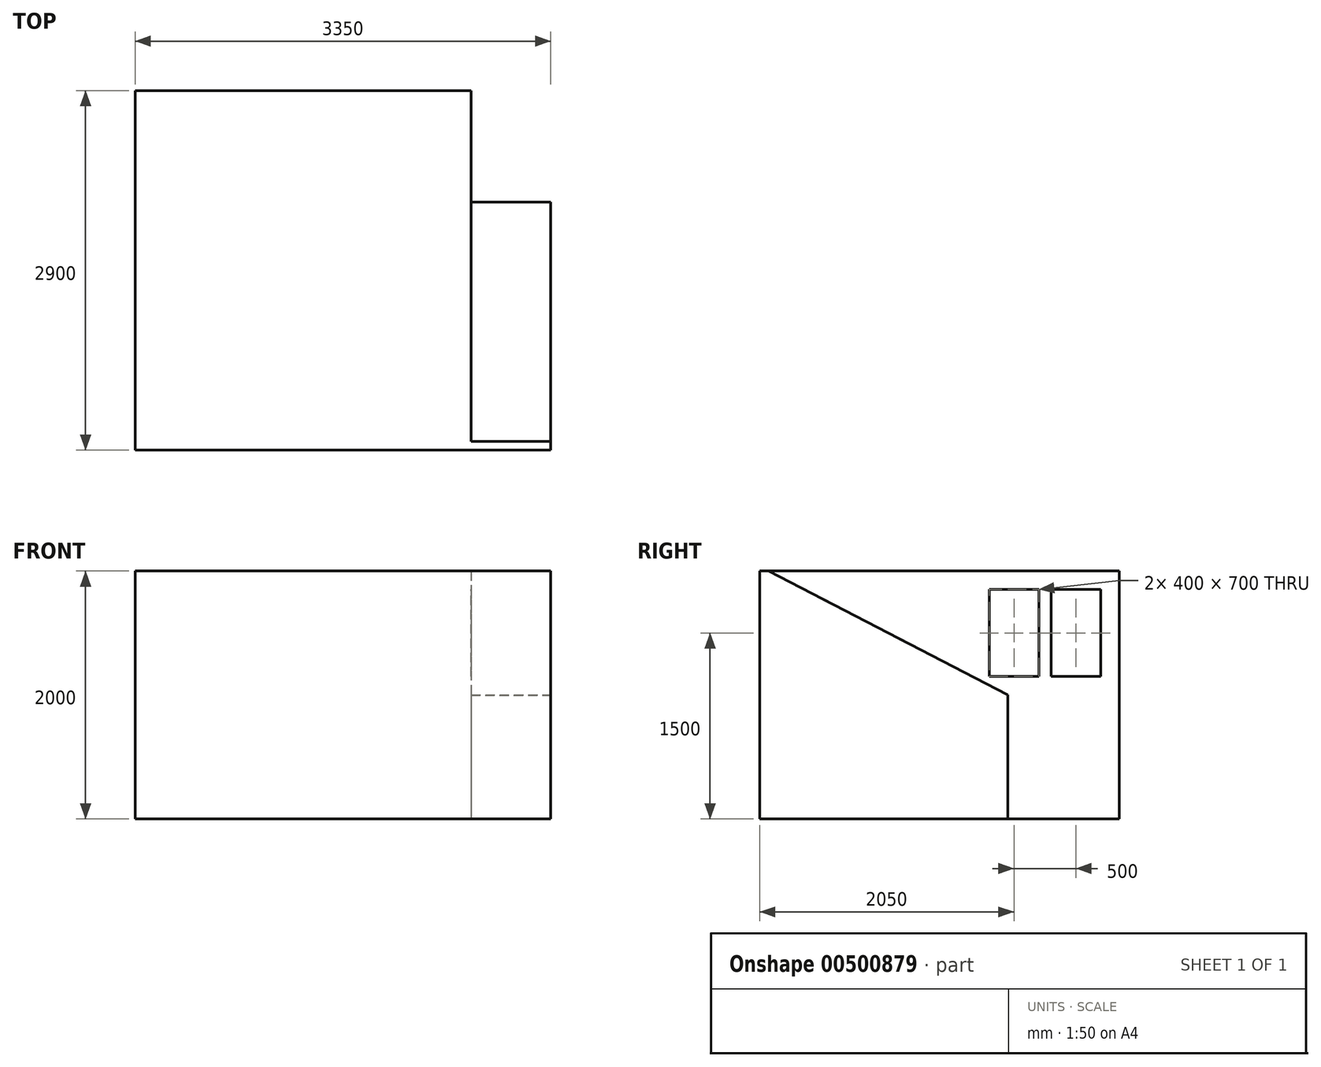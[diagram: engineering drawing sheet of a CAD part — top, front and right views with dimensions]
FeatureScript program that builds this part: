
annotation { "Feature Type Name" : "Feature", "Feature Type Description" : "" }
export const myFeature = defineFeature(function(context is Context, id is Id, definition is map)
    precondition{}
    {
        {
            var Q0;
            Q0=qCreatedBy(makeId("Top.planeOp"),FACE);
            var sketch = newSketch(context, id + "F0", { "sketchPlane" : qUnion([Q0])});
            skLineSegment(sketch, "E0.bottom", {"start": v(0, 10.3) * mm, "end": v(3350, 10.3) * mm});
            skLineSegment(sketch, "E0.top", {"start": v(0, 2910.3) * mm, "end": v(3350, 2910.3) * mm});
            skLineSegment(sketch, "E0.left", {"start": v(0, 10.3) * mm, "end": v(0, 2910.3) * mm});
            skLineSegment(sketch, "E0.right", {"start": v(3350, 10.3) * mm, "end": v(3350, 2910.3) * mm});
            skSolve(sketch);
        }
        {
            var Q0;
            Q0 = qSketchRegion(id + "F0", true);
            extrude(context, id + "F1", {"entities" : qUnion([Q0]), "depth" : 2000 * mm, "offsetDistance" : 25 * mm});
        }
        {
            var Q0;
            Q0=makeQuery(id+"F1.opExtrude","CAP_FACE",FACE,{"disambiguationData":[OSD([sQuery(id+"F0.wireOp",EDGE,"E0.bottom"),sQuery(id+"F0.wireOp",EDGE,"E0.top"),sQuery(id+"F0.wireOp",EDGE,"E0.left"),sQuery(id+"F0.wireOp",EDGE,"E0.right")])],"isStart":false});
            var sketch = newSketch(context, id + "F2", { "sketchPlane" : qUnion([Q0])});
            skLineSegment(sketch, "E1", {"start": v(1030, 2910.3) * mm, "end": v(1030, 80.3) * mm});
            skLineSegment(sketch, "E2", {"start": v(1030, 80.3) * mm, "end": v(3350, 80.3) * mm});
            skLineSegment(sketch, "E3", {"start": v(2310, 2910.3) * mm, "end": v(2310, 2010.3) * mm});
            skLineSegment(sketch, "E4", {"start": v(2310, 2010.3) * mm, "end": v(3350, 2010.3) * mm});
            skLineSegment(sketch, "E5", {"start": v(1030, 80.3) * mm, "end": v(2310, 2010.3) * mm});
            skSolve(sketch);
        }
        {
            var Q0;
            Q0=sQuery(id+"F2.wireOp",EDGE,"E5");
            cPlane(context, id + "F3", {"entities" : qUnion([Q0]), "cplaneType" : CPlaneType.LINE_ANGLE, "offset" : 25 * mm, "angle" : 90 * degree, "width" : 150 * mm, "height" : 150 * mm});
        }
        {
            var Q0;
            Q0=makeQuery(id+"F1.opExtrude","SWEPT_FACE",FACE,{"disambiguationData":[OSD([sQuery(id+"F0.wireOp",EDGE,"E0.right")])]});
            var sketch = newSketch(context, id + "F4", { "sketchPlane" : qUnion([Q0])});
            skLineSegment(sketch, "E6", {"start": v(80.3, 2000) * mm, "end": v(2010.3, 1000) * mm});
            skLineSegment(sketch, "E7", {"start": v(2910.3, 1000) * mm, "end": v(2910.3, 2000) * mm});
            skLineSegment(sketch, "E8", {"start": v(2910.3, 2000) * mm, "end": v(80.3, 2000) * mm});
            skLineSegment(sketch, "E9", {"start": v(2010.3, 1000) * mm, "end": v(2010.3, 0) * mm});
            skLineSegment(sketch, "E10", {"start": v(2010.3, 0) * mm, "end": v(2910.3, 0) * mm});
            skLineSegment(sketch, "E11", {"start": v(2910.3, 0) * mm, "end": v(2910.3, 1000) * mm});
            skSolve(sketch);
        }
        {
            var Q0;
            Q0 = qSketchRegion(id + "F4", true);
            var Q1;
            Q1=qCreatedBy(id+"F3.planeOp",FACE);
            extrude(context, id + "F5", {"entities" : qUnion([Q0]), "operationType" : NewBodyOperationType.REMOVE, "endBound" : BoundingType.UP_TO_SURFACE, "oppositeDirection" : true, "depth" : 25 * mm, "endBoundEntityFace" : qUnion([Q1]), "offsetDistance" : 25 * mm});
        }
        {
            var Q0;
            Q0=makeQuery(id+"F1.opExtrude","SWEPT_FACE",FACE,{"disambiguationData":[OSD([sQuery(id+"F0.wireOp",EDGE,"E0.top")])]});
            var sketch = newSketch(context, id + "F6", { "sketchPlane" : qUnion([Q0])});
            skLineSegment(sketch, "E12", {"start": v(-1030, 2000) * mm, "end": v(-2310, 1000) * mm});
            skLineSegment(sketch, "E13", {"start": v(-2906.9, 2000) * mm, "end": v(-1030, 2000) * mm});
            skLineSegment(sketch, "E14", {"start": v(-2310, 1000) * mm, "end": v(-2310, 0) * mm});
            skLineSegment(sketch, "E15", {"start": v(-2310, 0) * mm, "end": v(-2906.9, 0) * mm});
            skLineSegment(sketch, "E16", {"start": v(-2906.9, 0) * mm, "end": v(-2906.9, 2000) * mm});
            skSolve(sketch);
        }
        {
            var Q0;
            Q0 = qSketchRegion(id + "F6", true);
            var Q1;
            Q1=qCreatedBy(id+"F3.planeOp",FACE);
            extrude(context, id + "F7", {"entities" : qUnion([Q0]), "operationType" : NewBodyOperationType.REMOVE, "endBound" : BoundingType.UP_TO_SURFACE, "oppositeDirection" : true, "depth" : 25 * mm, "endBoundEntityFace" : qUnion([Q1]), "offsetDistance" : 25 * mm});
        }
        {
            var Q0;
            Q0=makeQuery(id+"F1.opExtrude","SWEPT_FACE",FACE,{"disambiguationData":[OSD([sQuery(id+"F0.wireOp",EDGE,"E0.top")])]});
            var sketch = newSketch(context, id + "F8", { "sketchPlane" : qUnion([Q0])});
            skLineSegment(sketch, "E17", {"start": v(-1030, 2000) * mm, "end": v(-2310, 1000) * mm});
            skLineSegment(sketch, "E18", {"start": v(-2710, 2000) * mm, "end": v(-1030, 2000) * mm});
            skLineSegment(sketch, "E19", {"start": v(-2710, 2000) * mm, "end": v(-2710, 0) * mm});
            skLineSegment(sketch, "E20", {"start": v(-2710, 0) * mm, "end": v(-2310, 0) * mm});
            skLineSegment(sketch, "E21", {"start": v(-2310, 0) * mm, "end": v(-2310, 1000) * mm});
            skSolve(sketch);
        }
        {
            var Q0;
            Q0 = qSketchRegion(id + "F8", true);
            extrude(context, id + "F9", {"entities" : qUnion([Q0]), "operationType" : NewBodyOperationType.ADD, "endBound" : BoundingType.UP_TO_NEXT, "oppositeDirection" : true, "depth" : 25 * mm, "offsetDistance" : 25 * mm});
        }
        {
            var Q0;
            Q0=makeQuery(id+"F1.opExtrude","CAP_FACE",FACE,{"disambiguationData":[OSD([sQuery(id+"F0.wireOp",EDGE,"E0.bottom"),sQuery(id+"F0.wireOp",EDGE,"E0.top"),sQuery(id+"F0.wireOp",EDGE,"E0.left"),sQuery(id+"F0.wireOp",EDGE,"E0.right")])],"isStart":true});
            shell(context, id + "F10", {"entities" : qUnion([Q0]), "thickness" : 2.5 * mm});
        }
        {
            var Q0;
            Q0=makeQuery(id+"F9.opExtrude","SWEPT_FACE",FACE,{"disambiguationData":[OSD([sQuery(id+"F8.wireOp",EDGE,"E19")])]});
            var sketch = newSketch(context, id + "F11", { "sketchPlane" : qUnion([Q0])});
            skLineSegment(sketch, "E22.bottom", {"start": v(2760.3, 1850) * mm, "end": v(2360.3, 1850) * mm});
            skLineSegment(sketch, "E22.top", {"start": v(2760.3, 1150) * mm, "end": v(2360.3, 1150) * mm});
            skLineSegment(sketch, "E22.left", {"start": v(2760.3, 1850) * mm, "end": v(2760.3, 1150) * mm});
            skLineSegment(sketch, "E22.right", {"start": v(2360.3, 1850) * mm, "end": v(2360.3, 1150) * mm});
            skLineSegment(sketch, "E23.bottom", {"start": v(2260.3, 1850) * mm, "end": v(1860.3, 1850) * mm});
            skLineSegment(sketch, "E23.top", {"start": v(2260.3, 1150) * mm, "end": v(1860.3, 1150) * mm});
            skLineSegment(sketch, "E23.left", {"start": v(2260.3, 1850) * mm, "end": v(2260.3, 1150) * mm});
            skLineSegment(sketch, "E23.right", {"start": v(1860.3, 1850) * mm, "end": v(1860.3, 1150) * mm});
            skSolve(sketch);
        }
        {
            var Q0;
            Q0 = qSketchRegion(id + "F11", true);
            extrude(context, id + "F12", {"entities" : qUnion([Q0]), "operationType" : NewBodyOperationType.REMOVE, "endBound" : BoundingType.UP_TO_NEXT, "oppositeDirection" : true, "depth" : 25 * mm, "offsetDistance" : 25 * mm});
        }
    });
